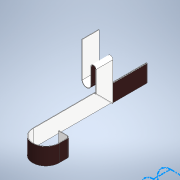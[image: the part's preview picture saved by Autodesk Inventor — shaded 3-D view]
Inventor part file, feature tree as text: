
AUTODESK INVENTOR PART (.ipt)
format: ipt  version: 2021 (Build 250183000, 183)  size: 204,288 bytes
history: native  units: mm
features: sketch x7, other x6, extrude x1
ambient origin geometry x8: Origin, YZ Plane, XZ Plane, XY Plane, X Axis, Y Axis, Z Axis, Center Point
bodies: Solid1 (feature_tree)
feature tree (14):
  extrude  "Extrusion1"  Depth=16.0mm
  other  "Bend Part1"
  other  "Bend Part13"
  other  "Bend Part14"
  other  "Bend Part15"
  other  "Bend Part16"
  other  "Bend Part17"
  sketch  "Sketch1"  dims[d0=300.0mm d1=16.0mm]
  sketch  "Sketch2"  dims[d2=0.5mm d3=0.0mm]
  sketch  "Sketch16"  dims[d4=8.0mm]
  sketch  "Sketch17"  dims[d5=1.0mm d6=90.0deg]
  sketch  "Sketch18"  dims[d50=10.0mm]
  sketch  "Sketch19"  dims[d51=12.0mm d52=180.0deg]
  sketch  "Sketch20"  dims[d53=45.0deg d54=130.0mm d55=0.1mm d56=180.0deg d57=28.0mm d58=0.1mm d59=180.0deg d60=20.0mm d61=2.0mm d62=180.0deg d63=15.0mm d64=4.0mm d65=180.0deg]
